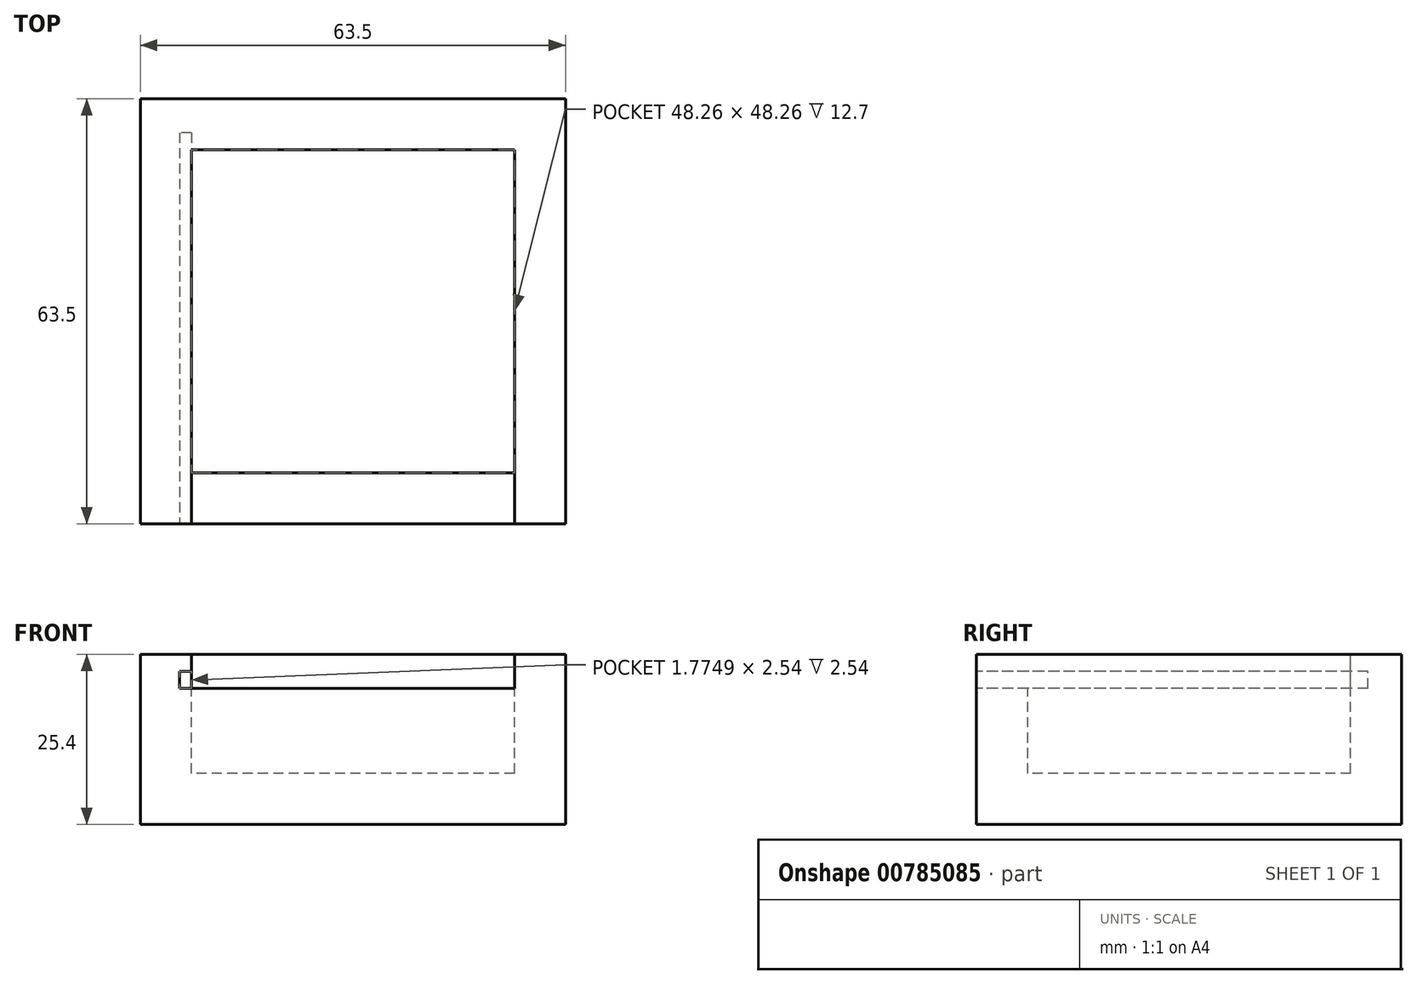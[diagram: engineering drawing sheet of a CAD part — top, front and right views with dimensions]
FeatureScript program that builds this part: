
annotation { "Feature Type Name" : "Feature", "Feature Type Description" : "" }
export const myFeature = defineFeature(function(context is Context, id is Id, definition is map)
    precondition{}
    {
        {
            var Q0;
            Q0=qCreatedBy(makeId("Top.planeOp"),FACE);
            var sketch = newSketch(context, id + "F0", { "sketchPlane" : qUnion([Q0])});
            skLineSegment(sketch, "E0.bottom", {"start": v(-45.74, 51.18) * mm, "end": v(17.76, 51.18) * mm});
            skLineSegment(sketch, "E0.top", {"start": v(-45.74, -12.32) * mm, "end": v(17.76, -12.32) * mm});
            skLineSegment(sketch, "E0.left", {"start": v(-45.74, 51.18) * mm, "end": v(-45.74, -12.32) * mm});
            skLineSegment(sketch, "E0.right", {"start": v(17.76, 51.18) * mm, "end": v(17.76, -12.32) * mm});
            skSolve(sketch);
        }
        {
            var Q0;
            Q0 = qSketchRegion(id + "F0", true);
            extrude(context, id + "F1", {"entities" : qUnion([Q0]), "depth" : 25.4 * mm, "offsetDistance" : 25.4 * mm});
        }
        {
            var Q0;
            Q0=makeQuery(id+"F1.opExtrude","CAP_FACE",FACE,{"disambiguationData":[OSD([sQuery(id+"F0.wireOp",EDGE,"E0.bottom"),sQuery(id+"F0.wireOp",EDGE,"E0.top"),sQuery(id+"F0.wireOp",EDGE,"E0.left"),sQuery(id+"F0.wireOp",EDGE,"E0.right")])],"isStart":false});
            var sketch = newSketch(context, id + "F2", { "sketchPlane" : qUnion([Q0])});
            skLineSegment(sketch, "E1", {"start": v(-38.12, 43.56) * mm, "end": v(-38.12, -4.7) * mm});
            skLineSegment(sketch, "E2", {"start": v(-38.12, -4.7) * mm, "end": v(10.14, -4.7) * mm});
            skLineSegment(sketch, "E3", {"start": v(10.14, -4.7) * mm, "end": v(10.14, 43.56) * mm});
            skLineSegment(sketch, "E4", {"start": v(10.14, 43.56) * mm, "end": v(-38.12, 43.56) * mm});
            skSolve(sketch);
        }
        {
            var Q0;
            Q0 = qSketchRegion(id + "F2", true);
            extrude(context, id + "F3", {"entities" : qUnion([Q0]), "operationType" : NewBodyOperationType.REMOVE, "oppositeDirection" : true, "depth" : 17.78 * mm, "offsetDistance" : 25.4 * mm});
        }
        {
            var Q0;
            Q0=makeQuery(id+"F1.opExtrude","CAP_FACE",FACE,{"disambiguationData":[OSD([sQuery(id+"F0.wireOp",EDGE,"E0.bottom"),sQuery(id+"F0.wireOp",EDGE,"E0.top"),sQuery(id+"F0.wireOp",EDGE,"E0.left"),sQuery(id+"F0.wireOp",EDGE,"E0.right")])],"isStart":false});
            var sketch = newSketch(context, id + "F4", { "sketchPlane" : qUnion([Q0])});
            skLineSegment(sketch, "E5", {"start": v(-38.12, -4.7) * mm, "end": v(-38.12, -12.32) * mm});
            skLineSegment(sketch, "E6", {"start": v(10.14, -4.7) * mm, "end": v(10.14, -12.32) * mm});
            skLineSegment(sketch, "E7", {"start": v(10.14, -12.32) * mm, "end": v(-38.12, -12.32) * mm});
            skLineSegment(sketch, "E8", {"start": v(-38.12, -4.7) * mm, "end": v(10.14, -4.7) * mm});
            skSolve(sketch);
        }
        {
            var Q0;
            Q0 = qSketchRegion(id + "F4", true);
            extrude(context, id + "F5", {"entities" : qUnion([Q0]), "operationType" : NewBodyOperationType.REMOVE, "oppositeDirection" : true, "depth" : 5.08 * mm, "offsetDistance" : 25.4 * mm});
        }
        {
            var Q0;
            Q0=makeQuery(id+"F1.opExtrude","SWEPT_FACE",FACE,{"disambiguationData":[OSD([sQuery(id+"F0.wireOp",EDGE,"E0.top")])]});
            var sketch = newSketch(context, id + "F6", { "sketchPlane" : qUnion([Q0])});
            skLineSegment(sketch, "E9", {"start": v(-38.12, 20.32) * mm, "end": v(-39.9, 20.32) * mm});
            skLineSegment(sketch, "E10", {"start": v(-39.9, 20.32) * mm, "end": v(-39.9, 22.86) * mm});
            skLineSegment(sketch, "E11", {"start": v(-39.9, 22.86) * mm, "end": v(-38.12, 22.86) * mm});
            skLineSegment(sketch, "E12", {"start": v(-38.12, 22.86) * mm, "end": v(-38.12, 20.32) * mm});
            skSolve(sketch);
        }
        {
            var Q0;
            Q0 = qSketchRegion(id + "F6", true);
            extrude(context, id + "F7", {"entities" : qUnion([Q0]), "operationType" : NewBodyOperationType.REMOVE, "oppositeDirection" : true, "depth" : 58.42 * mm, "offsetDistance" : 25.4 * mm});
        }
    });
